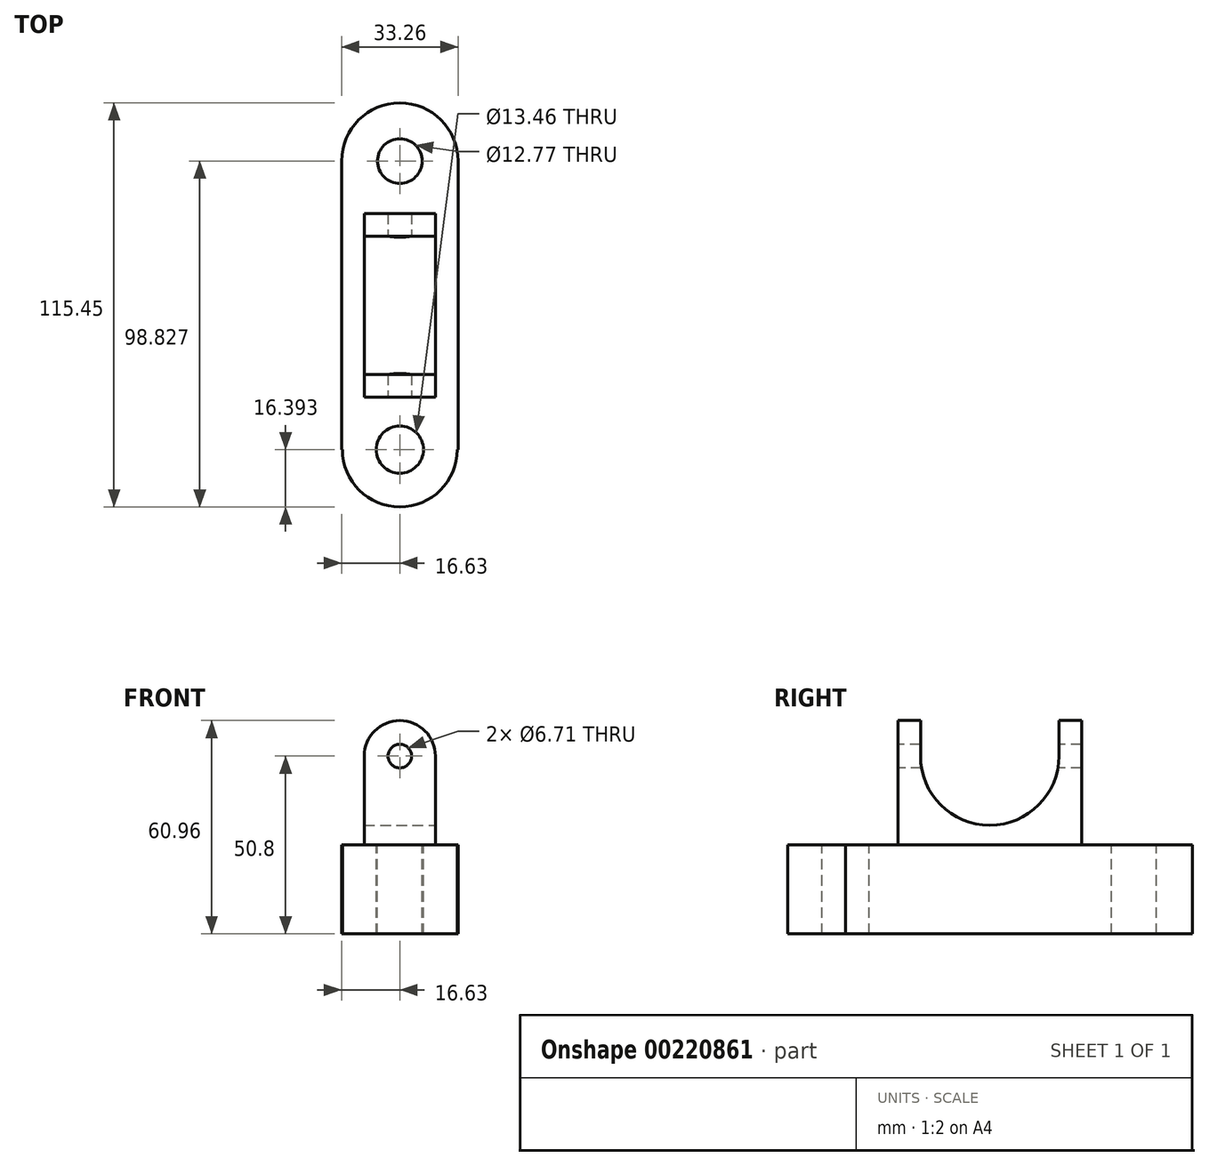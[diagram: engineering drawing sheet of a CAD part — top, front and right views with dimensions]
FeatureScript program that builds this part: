
annotation { "Feature Type Name" : "Feature", "Feature Type Description" : "" }
export const myFeature = defineFeature(function(context is Context, id is Id, definition is map)
    precondition{}
    {
        {
            var Q0;
            Q0=qCreatedBy(makeId("Top.planeOp"),FACE);
            var sketch = newSketch(context, id + "F0", { "sketchPlane" : qUnion([Q0])});
            skLineSegment(sketch, "E0.bottom", {"start": v(-16.63, 41.22) * mm, "end": v(16.63, 41.22) * mm});
            skLineSegment(sketch, "E0.top", {"start": v(-16.63, -41.22) * mm, "end": v(16.63, -41.22) * mm});
            skLineSegment(sketch, "E0.left", {"start": v(-16.63, 41.22) * mm, "end": v(-16.63, -41.22) * mm});
            skLineSegment(sketch, "E0.right", {"start": v(16.63, 41.22) * mm, "end": v(16.63, -41.22) * mm});
            skPoint(sketch, "E0.middle", {"position": v(0, 0) * mm});
            skSolve(sketch);
        }
        {
            var Q0;
            Q0=qCreatedBy(makeId("Top.planeOp"),FACE);
            var sketch = newSketch(context, id + "F1", { "sketchPlane" : qUnion([Q0])});
            skCircle(sketch, "E1", {"center": v(0, 41.22) * mm, "radius": 16.63 * mm});
            skSolve(sketch);
        }
        {
            var Q0;
            Q0=qCreatedBy(makeId("Top.planeOp"),FACE);
            var sketch = newSketch(context, id + "F2", { "sketchPlane" : qUnion([Q0])});
            skCircle(sketch, "E2", {"center": v(0, -41.22) * mm, "radius": 16.4 * mm});
            skSolve(sketch);
        }
        {
            var Q0;
            Q0 = qSketchRegion(id + "F0", true);
            extrude(context, id + "F3", {"entities" : qUnion([Q0]), "depth" : 25.4 * mm});
        }
        {
            var Q0;
            Q0 = qSketchRegion(id + "F1", true);
            extrude(context, id + "F4", {"entities" : qUnion([Q0]), "operationType" : NewBodyOperationType.ADD, "depth" : 25.4 * mm});
        }
        {
            var Q0;
            Q0 = qSketchRegion(id + "F2", true);
            extrude(context, id + "F5", {"entities" : qUnion([Q0]), "operationType" : NewBodyOperationType.ADD, "depth" : 25.4 * mm});
        }
        {
            var Q0;
            Q0=makeQuery(id+"F5.boolean.opBoolean","MERGE",FACE,{"derivedFrom":[makeQuery(id+"F4.boolean.opBoolean","MERGE",FACE,{"derivedFrom":[makeQuery(id+"F3.opExtrude","CAP_FACE",FACE,{"disambiguationData":[OSD([sQuery(id+"F0.wireOp",EDGE,"E0.bottom"),sQuery(id+"F0.wireOp",EDGE,"E0.top"),sQuery(id+"F0.wireOp",EDGE,"E0.left"),sQuery(id+"F0.wireOp",EDGE,"E0.right")])],"isStart":false}),makeQuery(id+"F4.opExtrude","CAP_FACE",FACE,{"disambiguationData":[OSD([sQuery(id+"F1.wireOp",EDGE,"E1")])],"isStart":false})]}),makeQuery(id+"F5.opExtrude","CAP_FACE",FACE,{"disambiguationData":[OSD([sQuery(id+"F2.wireOp",EDGE,"E2")])],"isStart":false})]});
            var sketch = newSketch(context, id + "F6", { "sketchPlane" : qUnion([Q0])});
            skCircle(sketch, "E3", {"center": v(0, 41.22) * mm, "radius": 6.39 * mm});
            skCircle(sketch, "E4", {"center": v(0, -41.22) * mm, "radius": 6.73 * mm});
            skSolve(sketch);
        }
        {
            var Q0;
            Q0=makeQuery(id+"F6.imprint","IMPRINT",FACE,{"disambiguationData":[TD([[makeQuery(id+"F6.imprint","IMPRINT",EDGE,{"derivedFrom":sQuery(id+"F6.wireOp",EDGE,"E3")}),1.0]])]});
            var Q1;
            Q1=makeQuery(id+"F6.imprint","IMPRINT",FACE,{"disambiguationData":[TD([[makeQuery(id+"F6.imprint","IMPRINT",EDGE,{"derivedFrom":sQuery(id+"F6.wireOp",EDGE,"E4")}),1.0]])]});
            extrude(context, id + "F7", {"entities" : qUnion([Q0, Q1]), "operationType" : NewBodyOperationType.REMOVE, "endBound" : BoundingType.THROUGH_ALL, "oppositeDirection" : true, "depth" : 25.4 * mm});
        }
        {
            var Q0;
            Q0=qCreatedBy(makeId("Top.planeOp"),FACE);
            var sketch = newSketch(context, id + "F8", { "sketchPlane" : qUnion([Q0])});
            skLineSegment(sketch, "E5.bottom", {"start": v(-10.16, 26.2) * mm, "end": v(10.16, 26.2) * mm});
            skLineSegment(sketch, "E5.top", {"start": v(-10.16, -26.2) * mm, "end": v(10.16, -26.2) * mm});
            skLineSegment(sketch, "E5.left", {"start": v(-10.16, 26.2) * mm, "end": v(-10.16, -26.2) * mm});
            skLineSegment(sketch, "E5.right", {"start": v(10.16, 26.2) * mm, "end": v(10.16, -26.2) * mm});
            skPoint(sketch, "E5.middle", {"position": v(0, 0) * mm});
            skSolve(sketch);
        }
        {
            var Q0;
            Q0 = qSketchRegion(id + "F8", true);
            extrude(context, id + "F9", {"entities" : qUnion([Q0]), "operationType" : NewBodyOperationType.ADD, "depth" : 50.8 * mm});
        }
        {
            var Q0;
            Q0=makeQuery(id+"F9.opExtrude","SWEPT_FACE",FACE,{"disambiguationData":[OSD([sQuery(id+"F8.wireOp",EDGE,"E5.right")])]});
            var sketch = newSketch(context, id + "F10", { "sketchPlane" : qUnion([Q0])});
            skCircle(sketch, "E6", {"center": v(0, 50.8) * mm, "radius": 19.76 * mm});
            skSolve(sketch);
        }
        {
            var Q0;
            {var subQ0=sQuery(id+"F10.wireOp",EDGE,"E6");var subQ1=makeQuery(id+"F9.opExtrude","CAP_EDGE",EDGE,{"disambiguationData":[OSD([sQuery(id+"F8.wireOp",EDGE,"E5.right")])],"isStart":false});var subQ2=makeQuery(id+"F10.imprint","INTERSECT",VERTEX,{"disambiguationData":[OD(0.0)],"derivedFrom":[subQ1,subQ0]});Q0=makeQuery(id+"F10.imprint","IMPRINT",FACE,{"disambiguationData":[TD([[makeQuery(id+"F10.imprint","IMPRINT",EDGE,{"disambiguationData":[TD([[subQ2,1.0]])],"derivedFrom":subQ0}),1.0]])]});}
            var Q1;
            {var subQ0=sQuery(id+"F10.wireOp",EDGE,"E6");var subQ1=makeQuery(id+"F9.opExtrude","CAP_EDGE",EDGE,{"disambiguationData":[OSD([sQuery(id+"F8.wireOp",EDGE,"E5.right")])],"isStart":false});var subQ2=makeQuery(id+"F10.imprint","INTERSECT",VERTEX,{"disambiguationData":[OD(0.0)],"derivedFrom":[subQ1,subQ0]});Q1=makeQuery(id+"F10.imprint","IMPRINT",FACE,{"disambiguationData":[TD([[makeQuery(id+"F10.imprint","IMPRINT",EDGE,{"disambiguationData":[TD([[subQ2,-1.0]])],"derivedFrom":subQ0}),1.0]])]});}
            extrude(context, id + "F11", {"entities" : qUnion([Q0, Q1]), "operationType" : NewBodyOperationType.REMOVE, "endBound" : BoundingType.THROUGH_ALL, "oppositeDirection" : true, "depth" : 25.4 * mm});
        }
        {
            var Q0;
            {var subQ0=sQuery(id+"F8.wireOp",EDGE,"E5.bottom");var subQ1=sQuery(id+"F8.wireOp",EDGE,"E5.left");var subQ2=sQuery(id+"F8.wireOp",EDGE,"E5.right");Q0=makeQuery(id+"F11.boolean.opBoolean","SPLIT",FACE,{"disambiguationData":[TD([makeQuery(id+"F9.opExtrude","SWEPT_FACE",FACE,{"disambiguationData":[OSD([subQ0])]})])],"derivedFrom":makeQuery(id+"F9.opExtrude","CAP_FACE",FACE,{"disambiguationData":[OSD([subQ0,sQuery(id+"F8.wireOp",EDGE,"E5.top"),subQ1,subQ2])],"isStart":false})});}
            var sketch = newSketch(context, id + "F12", { "sketchPlane" : qUnion([Q0])});
            skLineSegment(sketch, "E7.bottom", {"start": v(10.16, 26.2) * mm, "end": v(0, 26.2) * mm});
            skLineSegment(sketch, "E7.top", {"start": v(10.16, 19.76) * mm, "end": v(0, 19.76) * mm});
            skLineSegment(sketch, "E7.left", {"start": v(10.16, 26.2) * mm, "end": v(10.16, 19.76) * mm});
            skLineSegment(sketch, "E7.right", {"start": v(0, 26.2) * mm, "end": v(0, 19.76) * mm});
            skSolve(sketch);
        }
        {
            var Q0;
            Q0=makeQuery(id+"F12.imprint","IMPRINT",FACE,{"disambiguationData":[TD([[makeQuery(id+"F12.imprint","IMPRINT",EDGE,{"derivedFrom":sQuery(id+"F12.wireOp",EDGE,"E7.bottom")}),-1.0]])]});
            var Q1;
            Q1=sQuery(id+"F12.wireOp",EDGE,"E7.right");
            revolve(context, id + "F13", {"operationType" : NewBodyOperationType.ADD, "entities" : qUnion([Q0]), "axis" : qUnion([Q1]), "revolveType" : RevolveType.FULL});
        }
        {
            var Q0;
            {var subQ0=sQuery(id+"F8.wireOp",EDGE,"E5.top");var subQ1=sQuery(id+"F8.wireOp",EDGE,"E5.left");var subQ2=sQuery(id+"F8.wireOp",EDGE,"E5.right");Q0=makeQuery(id+"F11.boolean.opBoolean","SPLIT",FACE,{"disambiguationData":[TD([makeQuery(id+"F9.opExtrude","SWEPT_FACE",FACE,{"disambiguationData":[OSD([subQ0])]})])],"derivedFrom":makeQuery(id+"F9.opExtrude","CAP_FACE",FACE,{"disambiguationData":[OSD([sQuery(id+"F8.wireOp",EDGE,"E5.bottom"),subQ0,subQ1,subQ2])],"isStart":false})});}
            var sketch = newSketch(context, id + "F14", { "sketchPlane" : qUnion([Q0])});
            skLineSegment(sketch, "E8.bottom", {"start": v(-10.16, -26.2) * mm, "end": v(0, -26.2) * mm});
            skLineSegment(sketch, "E8.top", {"start": v(-10.16, -19.76) * mm, "end": v(0, -19.76) * mm});
            skLineSegment(sketch, "E8.left", {"start": v(-10.16, -26.2) * mm, "end": v(-10.16, -19.76) * mm});
            skLineSegment(sketch, "E8.right", {"start": v(0, -26.2) * mm, "end": v(0, -19.76) * mm});
            skSolve(sketch);
        }
        {
            var Q0;
            Q0=makeQuery(id+"F14.imprint","IMPRINT",FACE,{"disambiguationData":[TD([[makeQuery(id+"F14.imprint","IMPRINT",EDGE,{"derivedFrom":sQuery(id+"F14.wireOp",EDGE,"E8.bottom")}),1.0]])]});
            var Q1;
            Q1=sQuery(id+"F14.wireOp",EDGE,"E8.right");
            revolve(context, id + "F15", {"operationType" : NewBodyOperationType.ADD, "entities" : qUnion([Q0]), "axis" : qUnion([Q1]), "revolveType" : RevolveType.FULL});
        }
        {
            var Q0;
            Q0=makeQuery(id+"F15.boolean.opBoolean","MERGE",FACE,{"derivedFrom":[makeQuery(id+"F9.opExtrude","SWEPT_FACE",FACE,{"disambiguationData":[OSD([sQuery(id+"F8.wireOp",EDGE,"E5.top")])]}),makeQuery(id+"F15.opRevolve","SWEPT_FACE",FACE,{"disambiguationData":[OSD([sQuery(id+"F14.wireOp",EDGE,"E8.bottom")])]})]});
            var sketch = newSketch(context, id + "F16", { "sketchPlane" : qUnion([Q0])});
            skCircle(sketch, "E9", {"center": v(0, 50.8) * mm, "radius": 3.36 * mm});
            skSolve(sketch);
        }
        {
            var Q0;
            Q0=makeQuery(id+"F16.imprint","IMPRINT",FACE,{"disambiguationData":[TD([[makeQuery(id+"F16.imprint","IMPRINT",EDGE,{"derivedFrom":sQuery(id+"F16.wireOp",EDGE,"E9")}),1.0]])]});
            extrude(context, id + "F17", {"entities" : qUnion([Q0]), "operationType" : NewBodyOperationType.REMOVE, "endBound" : BoundingType.THROUGH_ALL, "oppositeDirection" : true, "depth" : 25.4 * mm});
        }
    });
